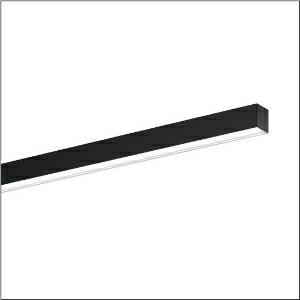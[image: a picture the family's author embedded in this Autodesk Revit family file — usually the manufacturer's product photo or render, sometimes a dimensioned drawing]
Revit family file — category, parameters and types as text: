
# Revit family: silica_r__21_51mx23da44bb_c0fe
name_source: partatom
category: Lighting Fixtures
units: mm (PartAtom-declared; Revit-internal decimal feet)

## family parameters
Cut with Voids When Loaded = No
Host = Face
Light Source = No
Part Type = Normal
Room Calculation Point = No
Round Connector Dimension = Use Diameter
Shared = No

## types (1)
- --- (1 x LED, 3280 lm, 22.4 W, 4000K)
    Apparent Load = 22 VA
    CIE Flux Codes = 78 96 99 100 100
    Color Rendering = 80
    Color Temperature = 4000K
    Default Elevation = 1800 mm
    Description = Silica® 21, office luminaire, primary optical cover: prismatic diffuser, of PMMA, CAT 2 (L<= 3000cd/m²), light emission: direct distribution, primary light characteristic: symmetric, installation type: surface-mounted, LED, rated luminous flux: 3.280lm, luminous efficacy: 146lm/W, light colour: 840, colour temperature: 4000K, control gear: DALI 2, with terminal, 3+2-pole, max. 2.5mm², mains connection: 220..240V, AC, 50/60Hz, rated input power: 22.4W, luminaire housing, of aluminium, matt jet black (RAL 9005), length: 1.204mm, width: 53mm, height: 53mm, protection rating (complete): IP20, insulation class (complete): insulation class I (protective earthing), certification: CE, permissible operating ambient temperature: 0..+35°C, standard: EN 50419, packaging unit: 1 piece
    Height = 53 mm
    Lamp = 1 x LED
    Lamp Light Flux = 3280 lm
    Lamp Power = 22.4 W
    Lamp count = 1
    Length = 1204 mm
    Luminous efficacy = 146 lm/W
    Manufacturer = Siteco
    ModVariant = No
    Model = 51MX23DA44BB
    Mounting Place = Ceiling
    Mounting Type = Surface mounted
    Number of Poles = 1
    OnlyDefault = Yes
    Power Factor = 1
    Product Name = Silica® 21
    Product group = office luminaire | ceiling mounted
    ProductGroupID = 302
    Protection Class = Protection class I
    Protection Degree = IP 20
    RLX_Detail_Level = 1
    RLX_Emergency_Light_Flux = 0 lm
    RLX_Emergency_Type = 0
    RLX_Emergency_Type_DB = No
    RlxData = <blob elided: 23753 chars, md5=96bcdad7>
    Socket = socket
    Standby Power = 0 W
    System Light Flux = 3280 lm
    System Power = 22 W
    Type Comments = factory setting: luminous flux: 100 % | dim-lin: 254 | 323 mA
    Type Image = l_1335925.jpg
    URL = http://relux.com
    VarID = @adj_007953
    Voltage = 0 V
    Weight = 0.00 kg
    Width = 53 mm

## geometry (parser evidence)
native form markers: Blend x4, Sweep x9
no freeform markers — native parametric forms only
